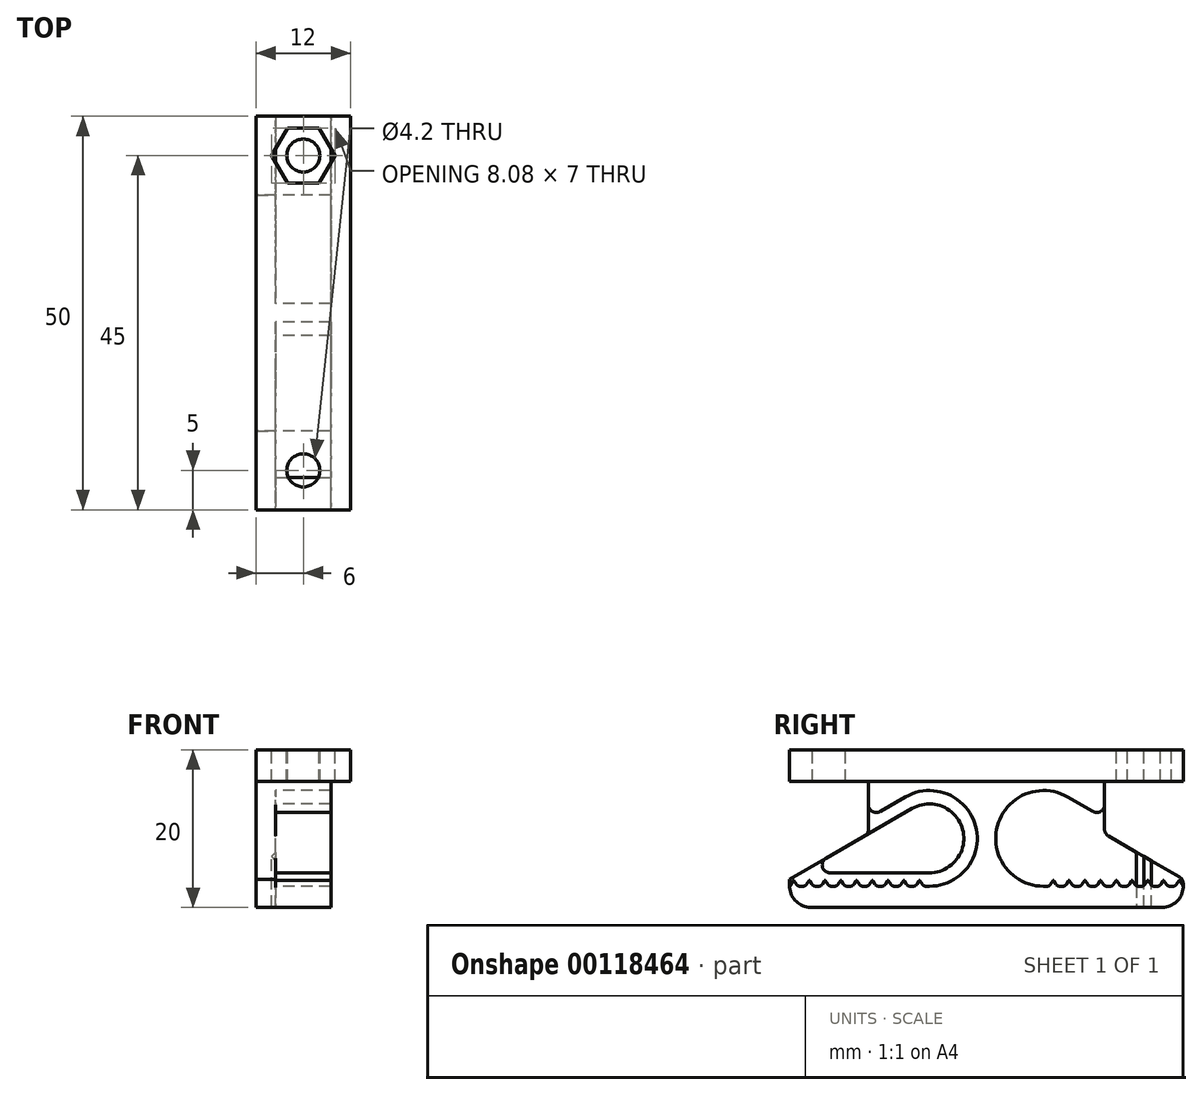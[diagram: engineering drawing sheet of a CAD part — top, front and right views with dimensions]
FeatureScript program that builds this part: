
annotation { "Feature Type Name" : "Feature", "Feature Type Description" : "" }
export const myFeature = defineFeature(function(context is Context, id is Id, definition is map)
    precondition{}
    {
        {
            var Q0;
            Q0=qCreatedBy(makeId("Right.planeOp"),FACE);
            var sketch = newSketch(context, id + "F0", { "sketchPlane" : qUnion([Q0])});
            skLineSegment(sketch, "E0", {"start": v(-25, 0) * mm, "end": v(25, 0) * mm});
            skPoint(sketch, "E1", {"position": v(0, 0) * mm});
            skPoint(sketch, "E2", {"position": v(-20, 0) * mm});
            skPoint(sketch, "E3.MirrorP", {"position": v(20, 0) * mm});
            skLineSegment(sketch, "E4", {"start": v(-25, -16) * mm, "end": v(25, -16) * mm, "construction": true});
            skCircle(sketch, "E5", {"center": v(-7.25, -11.25) * mm, "radius": 4.75 * mm, "construction": true});
            skLineSegment(sketch, "E6", {"start": v(-25, -16) * mm, "end": v(-9.63, -7.13) * mm, "construction": true});
            skCircle(sketch, "E7.MirrorC", {"center": v(7.25, -11.25) * mm, "radius": 4.75 * mm, "construction": true});
            skLineSegment(sketch, "E8.MirrorCS", {"start": v(25, -16) * mm, "end": v(9.63, -7.13) * mm, "construction": true});
            skLineSegment(sketch, "E9", {"start": v(-25, -4) * mm, "end": v(25, -4) * mm});
            skLineSegment(sketch, "E10", {"start": v(25, -4) * mm, "end": v(25, 0) * mm});
            skLineSegment(sketch, "E11.MirrorCS", {"start": v(-25, -4) * mm, "end": v(-25, 0) * mm});
            skLineSegment(sketch, "E12", {"start": v(-25, -20) * mm, "end": v(25, -20) * mm});
            skLineSegment(sketch, "E13", {"start": v(25, -20) * mm, "end": v(25, -16) * mm});
            skLineSegment(sketch, "E14", {"start": v(25, -16) * mm, "end": v(25, -4) * mm});
            skLineSegment(sketch, "E15.MirrorCS", {"start": v(-25, -16) * mm, "end": v(-25, -4) * mm});
            skLineSegment(sketch, "E16.MirrorCS", {"start": v(-25, -20) * mm, "end": v(-25, -16) * mm});
            skLineSegment(sketch, "E17", {"start": v(-15, 0) * mm, "end": v(-15, -20) * mm, "construction": true});
            skLineSegment(sketch, "E18.MirrorCS", {"start": v(15, 0) * mm, "end": v(15, -20) * mm, "construction": true});
            skSolve(sketch);
        }
        {
            var Q0;
            Q0=makeQuery(id+"F0.imprint","IMPRINT",FACE,{"disambiguationData":[TD([[makeQuery(id+"F0.imprint","IMPRINT",EDGE,{"derivedFrom":sQuery(id+"F0.wireOp",EDGE,"E0")}),-1.0]])]});
            extrude(context, id + "F1", {"entities" : qUnion([Q0]), "endBound" : BoundingType.SYMMETRIC, "depth" : 12 * mm});
        }
        {
            var Q0;
            Q0=makeQuery(id+"F0.imprint","IMPRINT",FACE,{"disambiguationData":[TD([[makeQuery(id+"F0.imprint","IMPRINT",EDGE,{"derivedFrom":sQuery(id+"F0.wireOp",EDGE,"E9")}),-1.0]])]});
            var Q1;
            Q1=makeQuery(id+"F1.opExtrude","CAP_FACE",FACE,{"disambiguationData":[OSD([sQuery(id+"F0.wireOp",EDGE,"E0"),sQuery(id+"F0.wireOp",EDGE,"E9"),sQuery(id+"F0.wireOp",EDGE,"E10"),sQuery(id+"F0.wireOp",EDGE,"E11.MirrorCS")])],"isStart":true});
            extrude(context, id + "F2", {"entities" : qUnion([Q0]), "operationType" : NewBodyOperationType.ADD, "endBound" : BoundingType.UP_TO_SURFACE, "oppositeDirection" : true, "endBoundEntityFace" : qUnion([Q1]), "depth" : 25 * mm, "hasSecondDirection" : true, "secondDirectionOppositeDirection" : true, "secondDirectionDepth" : 3.5 * mm});
        }
        {
            var Q0;
            Q0=qCreatedBy(makeId("Top.planeOp"),FACE);
            var sketch = newSketch(context, id + "F3", { "sketchPlane" : qUnion([Q0])});
            skCircle(sketch, "E19.cCircle", {"center": v(0, -20) * mm, "radius": 3.5 * mm, "construction": true});
            skLineSegment(sketch, "E19.0", {"start": v(4.04, -20) * mm, "end": v(2.02, -23.5) * mm});
            skLineSegment(sketch, "E19.1", {"start": v(2.02, -23.5) * mm, "end": v(-2.02, -23.5) * mm});
            skLineSegment(sketch, "E19.2", {"start": v(-2.02, -23.5) * mm, "end": v(-4.04, -20) * mm});
            skLineSegment(sketch, "E19.3", {"start": v(-4.04, -20) * mm, "end": v(-2.02, -16.5) * mm});
            skLineSegment(sketch, "E19.4", {"start": v(-2.02, -16.5) * mm, "end": v(2.02, -16.5) * mm});
            skLineSegment(sketch, "E19.5", {"start": v(2.02, -16.5) * mm, "end": v(4.04, -20) * mm});
            skPoint(sketch, "E19.0.midPoint", {"position": v(3.03, -21.75) * mm});
            skCircle(sketch, "E20", {"center": v(0, -20) * mm, "radius": 2.1 * mm});
            skLineSegment(sketch, "E21", {"start": v(2.02, -16.5) * mm, "end": v(6, -16.5) * mm});
            skLineSegment(sketch, "E22", {"start": v(6, -16.5) * mm, "end": v(6, -23.5) * mm});
            skLineSegment(sketch, "E23", {"start": v(6, -23.5) * mm, "end": v(2.02, -23.5) * mm});
            skLineSegment(sketch, "E24.MirrorCS", {"start": v(-4.04, 20) * mm, "end": v(-2.02, 16.5) * mm});
            skLineSegment(sketch, "E25.MirrorCS", {"start": v(-2.02, 16.5) * mm, "end": v(2.02, 16.5) * mm});
            skLineSegment(sketch, "E26.MirrorCS", {"start": v(2.02, 16.5) * mm, "end": v(6, 16.5) * mm});
            skLineSegment(sketch, "E27.MirrorCS", {"start": v(6, 16.5) * mm, "end": v(6, 23.5) * mm});
            skLineSegment(sketch, "E28.MirrorCS", {"start": v(6, 23.5) * mm, "end": v(2.02, 23.5) * mm});
            skLineSegment(sketch, "E29.MirrorCS", {"start": v(2.02, 23.5) * mm, "end": v(-2.02, 23.5) * mm});
            skLineSegment(sketch, "E30.MirrorCS", {"start": v(-2.02, 23.5) * mm, "end": v(-4.04, 20) * mm});
            skLineSegment(sketch, "E31.MirrorCS", {"start": v(4.04, 20) * mm, "end": v(2.02, 23.5) * mm});
            skLineSegment(sketch, "E32.MirrorCS", {"start": v(2.02, 16.5) * mm, "end": v(4.04, 20) * mm});
            skCircle(sketch, "E33.MirrorC", {"center": v(0, 20) * mm, "radius": 2.1 * mm});
            skSolve(sketch);
        }
        {
            var Q0;
            Q0=makeQuery(id+"F1.opExtrude","SWEPT_BODY",BODY,{"disambiguationData":[OSD([sQuery(id+"F0.wireOp",EDGE,"E0"),sQuery(id+"F0.wireOp",EDGE,"E9"),sQuery(id+"F0.wireOp",EDGE,"E10"),sQuery(id+"F0.wireOp",EDGE,"E11.MirrorCS")])]});
            transform(context, id + "F4", {"entities" : qUnion([Q0]), "transformType" : TransformType.COPY});
        }
        {
            var Q0;
            Q0=makeQuery(id+"F3.imprint","IMPRINT",FACE,{"disambiguationData":[TD([[makeQuery(id+"F3.imprint","IMPRINT",EDGE,{"derivedFrom":sQuery(id+"F3.wireOp",EDGE,"E20")}),1.0]])]});
            var Q1;
            Q1=makeQuery(id+"F3.imprint","IMPRINT",FACE,{"disambiguationData":[TD([[makeQuery(id+"F3.imprint","IMPRINT",EDGE,{"derivedFrom":sQuery(id+"F3.wireOp",EDGE,"E33.MirrorC")}),-1.0]])]});
            extrude(context, id + "F5", {"entities" : qUnion([Q0, Q1]), "operationType" : NewBodyOperationType.REMOVE, "endBound" : BoundingType.THROUGH_ALL, "oppositeDirection" : true, "depth" : 25 * mm});
        }
        {
            var Q0;
            Q0=qCreatedBy(makeId("Right.planeOp"),FACE);
            var sketch = newSketch(context, id + "F6", { "sketchPlane" : qUnion([Q0])});
            skLineSegment(sketch, "E34", {"start": v(-25, -16) * mm, "end": v(-9.63, -7.13) * mm, "construction": true});
            skLineSegment(sketch, "E35", {"start": v(-25, -16) * mm, "end": v(-7.25, -16) * mm, "construction": true});
            skArc(sketch, "E36", {"start": v(-9.63, -7.13) * mm, "mid": v(-11.85, -12.48) * mm, "end": v(-7.25, -16) * mm, "construction": true});
            skArc(sketch, "E37", {"start": v(-7.25, -16) * mm, "mid": v(-2.66, -10.01) * mm, "end": v(-9.63, -7.13) * mm, "construction": true});
            skLineSegment(sketch, "E38.0", {"start": v(-23.6, -15.62) * mm, "end": v(-9.44, -7.45) * mm});
            skLineSegment(sketch, "E38.1", {"start": v(-23.6, -15.62) * mm, "end": v(-7.25, -15.62) * mm});
            skArc(sketch, "E38.2", {"start": v(-7.25, -15.62) * mm, "mid": v(-3.02, -10.11) * mm, "end": v(-9.44, -7.45) * mm});
            skArc(sketch, "E39.MirrorCS", {"start": v(7.25, -15.62) * mm, "mid": v(3.02, -10.11) * mm, "end": v(9.44, -7.45) * mm});
            skLineSegment(sketch, "E40.MirrorCS", {"start": v(23.6, -15.62) * mm, "end": v(7.25, -15.62) * mm});
            skLineSegment(sketch, "E41.MirrorCS", {"start": v(23.6, -15.62) * mm, "end": v(9.44, -7.45) * mm});
            skLineSegment(sketch, "E42.0", {"start": v(-29.94, -17.32) * mm, "end": v(-15, -8.7) * mm, "construction": true});
            skLineSegment(sketch, "E42.1", {"start": v(-29.94, -17.32) * mm, "end": v(-25, -17.32) * mm, "construction": true});
            skArc(sketch, "E42.2", {"start": v(-7.25, -17.32) * mm, "mid": v(-1.38, -9.67) * mm, "end": v(-10.3, -5.98) * mm});
            skLineSegment(sketch, "E43", {"start": v(-15, -4) * mm, "end": v(15, -4) * mm});
            skLineSegment(sketch, "E44", {"start": v(-15, -4) * mm, "end": v(-15, -8.7) * mm});
            skLineSegment(sketch, "E45", {"start": v(-25, -17.32) * mm, "end": v(-25, -20) * mm});
            skLineSegment(sketch, "E46", {"start": v(-25, -20) * mm, "end": v(25, -20) * mm});
            skLineSegment(sketch, "E47", {"start": v(-15, -8.7) * mm, "end": v(-10.3, -5.98) * mm});
            skLineSegment(sketch, "E48", {"start": v(-25, -17.32) * mm, "end": v(-7.25, -17.32) * mm});
            skLineSegment(sketch, "E49.MirrorCS", {"start": v(25, -17.32) * mm, "end": v(25, -20) * mm});
            skLineSegment(sketch, "E50.MirrorCS", {"start": v(25, -17.32) * mm, "end": v(7.25, -17.32) * mm});
            skArc(sketch, "E51.MirrorCS", {"start": v(7.25, -17.32) * mm, "mid": v(1.38, -9.67) * mm, "end": v(10.3, -5.98) * mm});
            skLineSegment(sketch, "E52.MirrorCS", {"start": v(15, -8.7) * mm, "end": v(10.3, -5.98) * mm});
            skLineSegment(sketch, "E53.MirrorCS", {"start": v(15, -4) * mm, "end": v(15, -8.7) * mm});
            skArc(sketch, "E54", {"start": v(-25, -17.32) * mm, "mid": v(-24.22, -19.22) * mm, "end": v(-22.33, -20) * mm});
            skLineSegment(sketch, "E55", {"start": v(-24.5, -16.65) * mm, "end": v(-24.5, -17.32) * mm, "construction": true});
            skLineSegment(sketch, "E56", {"start": v(-25, -17.32) * mm, "end": v(-24.56, -16.61) * mm});
            skLineSegment(sketch, "E57.MirrorCS", {"start": v(-24, -17.32) * mm, "end": v(-24.44, -16.61) * mm});
            skArc(sketch, "E58", {"start": v(-24.56, -16.61) * mm, "mid": v(-24.5, -16.73) * mm, "end": v(-24.44, -16.61) * mm, "construction": true});
            skArc(sketch, "E59", {"start": v(-24.44, -16.61) * mm, "mid": v(-24.5, -16.58) * mm, "end": v(-24.56, -16.61) * mm});
            skLineSegment(sketch, "E60.1.0.0", {"start": v(-23, -17.33) * mm, "end": v(-22.56, -16.61) * mm});
            skArc(sketch, "E60.1.0.1", {"start": v(-22.44, -16.61) * mm, "mid": v(-22.5, -16.58) * mm, "end": v(-22.56, -16.61) * mm});
            skLineSegment(sketch, "E60.1.0.2", {"start": v(-22, -17.32) * mm, "end": v(-22.44, -16.61) * mm});
            skLineSegment(sketch, "E60.2.0.0", {"start": v(-21, -17.32) * mm, "end": v(-20.56, -16.61) * mm});
            skArc(sketch, "E60.2.0.1", {"start": v(-20.44, -16.61) * mm, "mid": v(-20.5, -16.58) * mm, "end": v(-20.56, -16.61) * mm});
            skLineSegment(sketch, "E60.2.0.2", {"start": v(-20, -17.32) * mm, "end": v(-20.44, -16.61) * mm});
            skLineSegment(sketch, "E60.3.0.0", {"start": v(-19, -17.32) * mm, "end": v(-18.56, -16.61) * mm});
            skArc(sketch, "E60.3.0.1", {"start": v(-18.44, -16.61) * mm, "mid": v(-18.5, -16.58) * mm, "end": v(-18.56, -16.61) * mm});
            skLineSegment(sketch, "E60.3.0.2", {"start": v(-18, -17.32) * mm, "end": v(-18.44, -16.61) * mm});
            skLineSegment(sketch, "E60.4.0.0", {"start": v(-17, -17.32) * mm, "end": v(-16.56, -16.61) * mm});
            skArc(sketch, "E60.4.0.1", {"start": v(-16.44, -16.61) * mm, "mid": v(-16.5, -16.58) * mm, "end": v(-16.56, -16.61) * mm});
            skLineSegment(sketch, "E60.4.0.2", {"start": v(-16, -17.32) * mm, "end": v(-16.44, -16.61) * mm});
            skLineSegment(sketch, "E60.5.0.0", {"start": v(-15, -17.32) * mm, "end": v(-14.56, -16.61) * mm});
            skArc(sketch, "E60.5.0.1", {"start": v(-14.44, -16.61) * mm, "mid": v(-14.5, -16.57) * mm, "end": v(-14.56, -16.61) * mm});
            skLineSegment(sketch, "E60.5.0.2", {"start": v(-14, -17.32) * mm, "end": v(-14.44, -16.61) * mm});
            skLineSegment(sketch, "E60.6.0.0", {"start": v(-13, -17.32) * mm, "end": v(-12.56, -16.61) * mm});
            skArc(sketch, "E60.6.0.1", {"start": v(-12.44, -16.61) * mm, "mid": v(-12.5, -16.57) * mm, "end": v(-12.56, -16.61) * mm});
            skLineSegment(sketch, "E60.6.0.2", {"start": v(-12, -17.32) * mm, "end": v(-12.44, -16.61) * mm});
            skLineSegment(sketch, "E60.7.0.0", {"start": v(-11, -17.32) * mm, "end": v(-10.56, -16.61) * mm});
            skArc(sketch, "E60.7.0.1", {"start": v(-10.44, -16.61) * mm, "mid": v(-10.5, -16.57) * mm, "end": v(-10.56, -16.61) * mm});
            skLineSegment(sketch, "E60.7.0.2", {"start": v(-10, -17.32) * mm, "end": v(-10.44, -16.61) * mm});
            skLineSegment(sketch, "E60.8.0.0", {"start": v(-9, -17.32) * mm, "end": v(-8.56, -16.61) * mm});
            skArc(sketch, "E60.8.0.1", {"start": v(-8.44, -16.61) * mm, "mid": v(-8.5, -16.57) * mm, "end": v(-8.56, -16.61) * mm});
            skLineSegment(sketch, "E60.8.0.2", {"start": v(-8, -17.32) * mm, "end": v(-8.44, -16.61) * mm});
            skLineSegment(sketch, "E60.direction1", {"start": v(-25, -17.32) * mm, "end": v(-23, -17.32) * mm, "construction": true});
            skArc(sketch, "E61.MirrorCS", {"start": v(25, -17.32) * mm, "mid": v(24.22, -19.22) * mm, "end": v(22.33, -20) * mm});
            skLineSegment(sketch, "E62.MirrorCS", {"start": v(25, -17.32) * mm, "end": v(24.56, -16.61) * mm});
            skArc(sketch, "E63.MirrorCS", {"start": v(24.44, -16.61) * mm, "mid": v(24.5, -16.58) * mm, "end": v(24.56, -16.61) * mm});
            skLineSegment(sketch, "E64.MirrorCS", {"start": v(24, -17.32) * mm, "end": v(24.44, -16.61) * mm});
            skLineSegment(sketch, "E65.MirrorCS", {"start": v(23, -17.33) * mm, "end": v(22.56, -16.61) * mm});
            skLineSegment(sketch, "E66.MirrorCS", {"start": v(22, -17.32) * mm, "end": v(22.44, -16.61) * mm});
            skLineSegment(sketch, "E67.MirrorCS", {"start": v(21, -17.32) * mm, "end": v(20.56, -16.61) * mm});
            skLineSegment(sketch, "E68.MirrorCS", {"start": v(20, -17.32) * mm, "end": v(20.44, -16.61) * mm});
            skArc(sketch, "E69.MirrorCS", {"start": v(20.44, -16.61) * mm, "mid": v(20.5, -16.58) * mm, "end": v(20.56, -16.61) * mm});
            skArc(sketch, "E70.MirrorCS", {"start": v(22.44, -16.61) * mm, "mid": v(22.5, -16.58) * mm, "end": v(22.56, -16.61) * mm});
            skLineSegment(sketch, "E71.MirrorCS", {"start": v(19, -17.32) * mm, "end": v(18.56, -16.61) * mm});
            skArc(sketch, "E72.MirrorCS", {"start": v(18.44, -16.61) * mm, "mid": v(18.5, -16.58) * mm, "end": v(18.56, -16.61) * mm});
            skLineSegment(sketch, "E73.MirrorCS", {"start": v(18, -17.32) * mm, "end": v(18.44, -16.61) * mm});
            skLineSegment(sketch, "E74.MirrorCS", {"start": v(17, -17.32) * mm, "end": v(16.56, -16.61) * mm});
            skArc(sketch, "E75.MirrorCS", {"start": v(16.44, -16.61) * mm, "mid": v(16.5, -16.58) * mm, "end": v(16.56, -16.61) * mm});
            skLineSegment(sketch, "E76.MirrorCS", {"start": v(16, -17.32) * mm, "end": v(16.44, -16.61) * mm});
            skLineSegment(sketch, "E77.MirrorCS", {"start": v(15, -17.32) * mm, "end": v(14.56, -16.61) * mm});
            skArc(sketch, "E78.MirrorCS", {"start": v(14.44, -16.61) * mm, "mid": v(14.5, -16.57) * mm, "end": v(14.56, -16.61) * mm});
            skLineSegment(sketch, "E79.MirrorCS", {"start": v(14, -17.32) * mm, "end": v(14.44, -16.61) * mm});
            skLineSegment(sketch, "E80.MirrorCS", {"start": v(13, -17.32) * mm, "end": v(12.56, -16.61) * mm});
            skArc(sketch, "E81.MirrorCS", {"start": v(12.44, -16.61) * mm, "mid": v(12.5, -16.57) * mm, "end": v(12.56, -16.61) * mm});
            skLineSegment(sketch, "E82.MirrorCS", {"start": v(12, -17.32) * mm, "end": v(12.44, -16.61) * mm});
            skLineSegment(sketch, "E83.MirrorCS", {"start": v(11, -17.32) * mm, "end": v(10.56, -16.61) * mm});
            skArc(sketch, "E84.MirrorCS", {"start": v(10.44, -16.61) * mm, "mid": v(10.5, -16.57) * mm, "end": v(10.56, -16.61) * mm});
            skLineSegment(sketch, "E85.MirrorCS", {"start": v(10, -17.32) * mm, "end": v(10.44, -16.61) * mm});
            skLineSegment(sketch, "E86.MirrorCS", {"start": v(9, -17.32) * mm, "end": v(8.56, -16.61) * mm});
            skArc(sketch, "E87.MirrorCS", {"start": v(8.44, -16.61) * mm, "mid": v(8.5, -16.57) * mm, "end": v(8.56, -16.61) * mm});
            skLineSegment(sketch, "E88.MirrorCS", {"start": v(8, -17.32) * mm, "end": v(8.44, -16.61) * mm});
            skLineSegment(sketch, "E89", {"start": v(-23.6, -15.62) * mm, "end": v(-25, -16.43) * mm});
            skLineSegment(sketch, "E90", {"start": v(-25, -16.43) * mm, "end": v(-25, -4) * mm});
            skLineSegment(sketch, "E91", {"start": v(-25, -4) * mm, "end": v(-15, -4) * mm});
            skLineSegment(sketch, "E92", {"start": v(-15, -8.7) * mm, "end": v(-15, -10.66) * mm});
            skLineSegment(sketch, "E93.MirrorCS", {"start": v(15, -8.7) * mm, "end": v(15, -10.66) * mm});
            skLineSegment(sketch, "E94.MirrorCS", {"start": v(25, -4) * mm, "end": v(15, -4) * mm});
            skLineSegment(sketch, "E95.MirrorCS", {"start": v(25, -16.43) * mm, "end": v(25, -4) * mm});
            skLineSegment(sketch, "E96.MirrorCS", {"start": v(23.6, -15.62) * mm, "end": v(25, -16.43) * mm});
            skSolve(sketch);
        }
        {
            var Q0;
            Q0=makeQuery(id+"F4.opPattern","COPY",BODY,{"derivedFrom":makeQuery(id+"F1.opExtrude","SWEPT_BODY",BODY,{"disambiguationData":[OSD([sQuery(id+"F0.wireOp",EDGE,"E0"),sQuery(id+"F0.wireOp",EDGE,"E9"),sQuery(id+"F0.wireOp",EDGE,"E10"),sQuery(id+"F0.wireOp",EDGE,"E11.MirrorCS")])]}),"instanceName":"1"});
            transform(context, id + "F7", {"entities" : qUnion([Q0]), "transformType" : TransformType.COPY});
        }
        {
            var Q0;
            {var subQ31=sQuery(id+"F6.wireOp",EDGE,"E42.2");Q0=makeQuery(id+"F6.imprint","IMPRINT",FACE,{"disambiguationData":[TD([[makeQuery(id+"F6.imprint","IMPRINT",EDGE,{"derivedFrom":subQ31}),-1.0]])]});}
            var Q1;
            Q1=makeQuery(id+"F6.imprint","IMPRINT",FACE,{"disambiguationData":[TD([[makeQuery(id+"F6.imprint","IMPRINT",EDGE,{"derivedFrom":sQuery(id+"F6.wireOp",EDGE,"E38.0")}),-1.0]])]});
            var Q2;
            Q2=makeQuery(id+"F6.imprint","IMPRINT",FACE,{"disambiguationData":[TD([[makeQuery(id+"F6.imprint","IMPRINT",EDGE,{"derivedFrom":sQuery(id+"F6.wireOp",EDGE,"E39.MirrorCS")}),-1.0]])]});
            var Q3;
            {var subQ0=sQuery(id+"F6.wireOp",EDGE,"E56");Q3=makeQuery(id+"F6.imprint","IMPRINT",FACE,{"disambiguationData":[TD([[makeQuery(id+"F6.imprint","IMPRINT",EDGE,{"derivedFrom":subQ0}),-1.0]])]});}
            var Q4;
            {var subQ0=sQuery(id+"F6.wireOp",EDGE,"E60.1.0.0");Q4=makeQuery(id+"F6.imprint","IMPRINT",FACE,{"disambiguationData":[TD([[makeQuery(id+"F6.imprint","IMPRINT",EDGE,{"derivedFrom":subQ0}),-1.0]])]});}
            var Q5;
            {var subQ0=sQuery(id+"F6.wireOp",EDGE,"E60.2.0.0");Q5=makeQuery(id+"F6.imprint","IMPRINT",FACE,{"disambiguationData":[TD([[makeQuery(id+"F6.imprint","IMPRINT",EDGE,{"derivedFrom":subQ0}),-1.0]])]});}
            var Q6;
            {var subQ0=sQuery(id+"F6.wireOp",EDGE,"E60.3.0.0");Q6=makeQuery(id+"F6.imprint","IMPRINT",FACE,{"disambiguationData":[TD([[makeQuery(id+"F6.imprint","IMPRINT",EDGE,{"derivedFrom":subQ0}),-1.0]])]});}
            var Q7;
            {var subQ0=sQuery(id+"F6.wireOp",EDGE,"E60.4.0.0");Q7=makeQuery(id+"F6.imprint","IMPRINT",FACE,{"disambiguationData":[TD([[makeQuery(id+"F6.imprint","IMPRINT",EDGE,{"derivedFrom":subQ0}),-1.0]])]});}
            var Q8;
            {var subQ0=sQuery(id+"F6.wireOp",EDGE,"E60.5.0.0");Q8=makeQuery(id+"F6.imprint","IMPRINT",FACE,{"disambiguationData":[TD([[makeQuery(id+"F6.imprint","IMPRINT",EDGE,{"derivedFrom":subQ0}),-1.0]])]});}
            var Q9;
            {var subQ0=sQuery(id+"F6.wireOp",EDGE,"E60.6.0.0");Q9=makeQuery(id+"F6.imprint","IMPRINT",FACE,{"disambiguationData":[TD([[makeQuery(id+"F6.imprint","IMPRINT",EDGE,{"derivedFrom":subQ0}),-1.0]])]});}
            var Q10;
            {var subQ0=sQuery(id+"F6.wireOp",EDGE,"E60.7.0.0");Q10=makeQuery(id+"F6.imprint","IMPRINT",FACE,{"disambiguationData":[TD([[makeQuery(id+"F6.imprint","IMPRINT",EDGE,{"derivedFrom":subQ0}),-1.0]])]});}
            var Q11;
            {var subQ0=sQuery(id+"F6.wireOp",EDGE,"E60.8.0.0");Q11=makeQuery(id+"F6.imprint","IMPRINT",FACE,{"disambiguationData":[TD([[makeQuery(id+"F6.imprint","IMPRINT",EDGE,{"derivedFrom":subQ0}),-1.0]])]});}
            var Q12;
            {var subQ0=sQuery(id+"F6.wireOp",EDGE,"E86.MirrorCS");Q12=makeQuery(id+"F6.imprint","IMPRINT",FACE,{"disambiguationData":[TD([[makeQuery(id+"F6.imprint","IMPRINT",EDGE,{"derivedFrom":subQ0}),1.0]])]});}
            var Q13;
            {var subQ0=sQuery(id+"F6.wireOp",EDGE,"E83.MirrorCS");Q13=makeQuery(id+"F6.imprint","IMPRINT",FACE,{"disambiguationData":[TD([[makeQuery(id+"F6.imprint","IMPRINT",EDGE,{"derivedFrom":subQ0}),1.0]])]});}
            var Q14;
            {var subQ0=sQuery(id+"F6.wireOp",EDGE,"E80.MirrorCS");Q14=makeQuery(id+"F6.imprint","IMPRINT",FACE,{"disambiguationData":[TD([[makeQuery(id+"F6.imprint","IMPRINT",EDGE,{"derivedFrom":subQ0}),1.0]])]});}
            var Q15;
            {var subQ0=sQuery(id+"F6.wireOp",EDGE,"E77.MirrorCS");Q15=makeQuery(id+"F6.imprint","IMPRINT",FACE,{"disambiguationData":[TD([[makeQuery(id+"F6.imprint","IMPRINT",EDGE,{"derivedFrom":subQ0}),1.0]])]});}
            var Q16;
            {var subQ0=sQuery(id+"F6.wireOp",EDGE,"E74.MirrorCS");Q16=makeQuery(id+"F6.imprint","IMPRINT",FACE,{"disambiguationData":[TD([[makeQuery(id+"F6.imprint","IMPRINT",EDGE,{"derivedFrom":subQ0}),1.0]])]});}
            var Q17;
            {var subQ0=sQuery(id+"F6.wireOp",EDGE,"E71.MirrorCS");Q17=makeQuery(id+"F6.imprint","IMPRINT",FACE,{"disambiguationData":[TD([[makeQuery(id+"F6.imprint","IMPRINT",EDGE,{"derivedFrom":subQ0}),1.0]])]});}
            var Q18;
            {var subQ0=sQuery(id+"F6.wireOp",EDGE,"E67.MirrorCS");Q18=makeQuery(id+"F6.imprint","IMPRINT",FACE,{"disambiguationData":[TD([[makeQuery(id+"F6.imprint","IMPRINT",EDGE,{"derivedFrom":subQ0}),1.0]])]});}
            var Q19;
            {var subQ0=sQuery(id+"F6.wireOp",EDGE,"E65.MirrorCS");Q19=makeQuery(id+"F6.imprint","IMPRINT",FACE,{"disambiguationData":[TD([[makeQuery(id+"F6.imprint","IMPRINT",EDGE,{"derivedFrom":subQ0}),1.0]])]});}
            var Q20;
            {var subQ0=sQuery(id+"F6.wireOp",EDGE,"E62.MirrorCS");Q20=makeQuery(id+"F6.imprint","IMPRINT",FACE,{"disambiguationData":[TD([[makeQuery(id+"F6.imprint","IMPRINT",EDGE,{"derivedFrom":subQ0}),1.0]])]});}
            extrude(context, id + "F8", {"entities" : qUnion([Q0, Q1, Q2, Q3, Q4, Q5, Q6, Q7, Q8, Q9, Q10, Q11, Q12, Q13, Q14, Q15, Q16, Q17, Q18, Q19, Q20]), "operationType" : NewBodyOperationType.ADD, "endBound" : BoundingType.SYMMETRIC, "depth" : 7 * mm});
        }
        {
            var Q0;
            {var subQ0=sQuery(id+"F6.wireOp",EDGE,"E45");Q0=makeQuery(id+"F6.imprint","IMPRINT",FACE,{"disambiguationData":[TD([[makeQuery(id+"F6.imprint","IMPRINT",EDGE,{"derivedFrom":subQ0}),1.0]])]});}
            var Q1;
            {var subQ0=sQuery(id+"F6.wireOp",EDGE,"E49.MirrorCS");Q1=makeQuery(id+"F6.imprint","IMPRINT",FACE,{"disambiguationData":[TD([[makeQuery(id+"F6.imprint","IMPRINT",EDGE,{"derivedFrom":subQ0}),-1.0]])]});}
            var Q2;
            Q2=makeQuery(id+"F6.imprint","IMPRINT",FACE,{"disambiguationData":[TD([[makeQuery(id+"F6.imprint","IMPRINT",EDGE,{"derivedFrom":sQuery(id+"F6.wireOp",EDGE,"E44")}),-1.0]])]});
            var Q3;
            Q3=makeQuery(id+"F6.imprint","IMPRINT",FACE,{"disambiguationData":[TD([[makeQuery(id+"F6.imprint","IMPRINT",EDGE,{"derivedFrom":sQuery(id+"F6.wireOp",EDGE,"E53.MirrorCS")}),1.0]])]});
            extrude(context, id + "F9", {"entities" : qUnion([Q0, Q1, Q2, Q3]), "operationType" : NewBodyOperationType.REMOVE, "endBound" : BoundingType.THROUGH_ALL, "oppositeDirection" : true, "depth" : 25 * mm});
        }
        {
            var Q0;
            Q0=makeQuery(id+"F8.opExtrude","SWEPT_EDGE",EDGE,{"disambiguationData":[OSD([sQuery(id+"F6.wireOp",EDGE,"E38.0"),sQuery(id+"F6.wireOp",EDGE,"E38.1")])]});
            var Q1;
            Q1=makeQuery(id+"F8.opExtrude","SWEPT_EDGE",EDGE,{"disambiguationData":[OSD([sQuery(id+"F6.wireOp",EDGE,"E40.MirrorCS"),sQuery(id+"F6.wireOp",EDGE,"E41.MirrorCS")])]});
            var Q2;
            Q2=makeQuery(id+"F8.opExtrude","SWEPT_EDGE",EDGE,{"disambiguationData":[OSD([sQuery(id+"F6.wireOp",EDGE,"E44"),sQuery(id+"F6.wireOp",EDGE,"E47")])]});
            var Q3;
            Q3=makeQuery(id+"F8.opExtrude","SWEPT_EDGE",EDGE,{"disambiguationData":[OSD([sQuery(id+"F6.wireOp",EDGE,"E52.MirrorCS"),sQuery(id+"F6.wireOp",EDGE,"E53.MirrorCS")])]});
            var Q4;
            Q4=makeQuery(id+"F8.opExtrude","SWEPT_EDGE",EDGE,{"disambiguationData":[OSD([sQuery(id+"F6.wireOp",EDGE,"E43"),sQuery(id+"F6.wireOp",EDGE,"E44")])]});
            var Q5;
            Q5=makeQuery(id+"F8.opExtrude","SWEPT_EDGE",EDGE,{"disambiguationData":[OSD([sQuery(id+"F6.wireOp",EDGE,"E43"),sQuery(id+"F6.wireOp",EDGE,"E53.MirrorCS")])]});
            var Q6;
            Q6=makeQuery(id+"F7.opPattern","COPY",EDGE,{"derivedFrom":makeQuery(id+"F4.opPattern","COPY",EDGE,{"derivedFrom":makeQuery(id+"F1.opExtrude","SWEPT_EDGE",EDGE,{"disambiguationData":[OSD([sQuery(id+"F0.wireOp",EDGE,"E9"),sQuery(id+"F0.wireOp",EDGE,"E11.MirrorCS"),sQuery(id+"F0.wireOp",EDGE,"E15.MirrorCS")])]}),"instanceName":"1"}),"instanceName":"1"});
            var Q7;
            Q7=makeQuery(id+"F7.opPattern","COPY",EDGE,{"derivedFrom":makeQuery(id+"F4.opPattern","COPY",EDGE,{"derivedFrom":makeQuery(id+"F1.opExtrude","SWEPT_EDGE",EDGE,{"disambiguationData":[OSD([sQuery(id+"F0.wireOp",EDGE,"E9"),sQuery(id+"F0.wireOp",EDGE,"E10"),sQuery(id+"F0.wireOp",EDGE,"E14")])]}),"instanceName":"1"}),"instanceName":"1"});
            var Q8;
            Q8=makeQuery(id+"F9.boolean.opBoolean","COPY",EDGE,{"derivedFrom":makeQuery(id+"F9.opExtrude","SWEPT_EDGE",EDGE,{"disambiguationData":[OSD([sQuery(id+"F6.wireOp",EDGE,"E89"),sQuery(id+"F6.wireOp",EDGE,"E90")])]})});
            var Q9;
            Q9=makeQuery(id+"F9.boolean.opBoolean","COPY",EDGE,{"derivedFrom":makeQuery(id+"F9.opExtrude","SWEPT_EDGE",EDGE,{"disambiguationData":[OSD([sQuery(id+"F6.wireOp",EDGE,"E95.MirrorCS"),sQuery(id+"F6.wireOp",EDGE,"E96.MirrorCS")])]})});
            var Q10;
            Q10=makeQuery(id+"F9.boolean.opBoolean","COPY",EDGE,{"derivedFrom":makeQuery(id+"F9.opExtrude","SWEPT_EDGE",EDGE,{"disambiguationData":[OSD([sQuery(id+"F6.wireOp",EDGE,"E38.0"),sQuery(id+"F6.wireOp",EDGE,"E92")])]})});
            var Q11;
            Q11=makeQuery(id+"F9.boolean.opBoolean","COPY",EDGE,{"derivedFrom":makeQuery(id+"F9.opExtrude","SWEPT_EDGE",EDGE,{"disambiguationData":[OSD([sQuery(id+"F6.wireOp",EDGE,"E41.MirrorCS"),sQuery(id+"F6.wireOp",EDGE,"E93.MirrorCS")])]})});
            fillet(context, id + "F10", {"entities" : qUnion([Q0, Q1, Q2, Q3, Q4, Q5, Q6, Q7, Q8, Q9, Q10, Q11]), "radius" : 1 * mm, "tangentPropagation" : true, "allowEdgeOverflow" : false});
        }
        {
            var Q0;
            Q0=makeQuery(id+"F7.opPattern","COPY",EDGE,{"derivedFrom":makeQuery(id+"FzJrt3O1qZVC5p7_1.boolean.opBoolean","INTERSECT",EDGE,{"derivedFrom":[makeQuery(id+"F4.opPattern","COPY",FACE,{"derivedFrom":makeQuery(id+"F1.opExtrude","SWEPT_FACE",FACE,{"disambiguationData":[OSD([sQuery(id+"F0.wireOp",EDGE,"E9")])]}),"instanceName":"1"}),makeQuery(id+"FzJrt3O1qZVC5p7_1.opExtrude","SWEPT_FACE",FACE,{"disambiguationData":[OSD([sQuery(id+"F3.wireOp",EDGE,"E19.1"),sQuery(id+"F3.wireOp",EDGE,"E23")])]})]}),"instanceName":"1"});
            var Q1;
            Q1=makeQuery(id+"F7.opPattern","COPY",EDGE,{"derivedFrom":makeQuery(id+"FzJrt3O1qZVC5p7_1.boolean.opBoolean","INTERSECT",EDGE,{"derivedFrom":[makeQuery(id+"F4.opPattern","COPY",FACE,{"derivedFrom":makeQuery(id+"F1.opExtrude","SWEPT_FACE",FACE,{"disambiguationData":[OSD([sQuery(id+"F0.wireOp",EDGE,"E9")])]}),"instanceName":"1"}),makeQuery(id+"FzJrt3O1qZVC5p7_1.opExtrude","SWEPT_FACE",FACE,{"disambiguationData":[OSD([sQuery(id+"F3.wireOp",EDGE,"E19.4"),sQuery(id+"F3.wireOp",EDGE,"E21")])]})]}),"instanceName":"1"});
            var Q2;
            Q2=makeQuery(id+"F7.opPattern","COPY",EDGE,{"derivedFrom":makeQuery(id+"FzJrt3O1qZVC5p7_1.boolean.opBoolean","INTERSECT",EDGE,{"derivedFrom":[makeQuery(id+"F4.opPattern","COPY",FACE,{"derivedFrom":makeQuery(id+"F1.opExtrude","SWEPT_FACE",FACE,{"disambiguationData":[OSD([sQuery(id+"F0.wireOp",EDGE,"E9")])]}),"instanceName":"1"}),makeQuery(id+"FzJrt3O1qZVC5p7_1.opExtrude","SWEPT_FACE",FACE,{"disambiguationData":[OSD([sQuery(id+"F3.wireOp",EDGE,"E19.2")])]})]}),"instanceName":"1"});
            var Q3;
            Q3=makeQuery(id+"F7.opPattern","COPY",EDGE,{"derivedFrom":makeQuery(id+"FzJrt3O1qZVC5p7_1.boolean.opBoolean","INTERSECT",EDGE,{"derivedFrom":[makeQuery(id+"F4.opPattern","COPY",FACE,{"derivedFrom":makeQuery(id+"F1.opExtrude","SWEPT_FACE",FACE,{"disambiguationData":[OSD([sQuery(id+"F0.wireOp",EDGE,"E9")])]}),"instanceName":"1"}),makeQuery(id+"FzJrt3O1qZVC5p7_1.opExtrude","SWEPT_FACE",FACE,{"disambiguationData":[OSD([sQuery(id+"F3.wireOp",EDGE,"E19.3")])]})]}),"instanceName":"1"});
            var Q4;
            Q4=makeQuery(id+"F7.opPattern","COPY",EDGE,{"derivedFrom":makeQuery(id+"FzJrt3O1qZVC5p7_1.boolean.opBoolean","INTERSECT",EDGE,{"derivedFrom":[makeQuery(id+"F4.opPattern","COPY",FACE,{"derivedFrom":makeQuery(id+"F1.opExtrude","SWEPT_FACE",FACE,{"disambiguationData":[OSD([sQuery(id+"F0.wireOp",EDGE,"E9")])]}),"instanceName":"1"}),makeQuery(id+"FzJrt3O1qZVC5p7_1.opExtrude","SWEPT_FACE",FACE,{"disambiguationData":[OSD([sQuery(id+"F3.wireOp",EDGE,"E25.MirrorCS"),sQuery(id+"F3.wireOp",EDGE,"E26.MirrorCS")])]})]}),"instanceName":"1"});
            var Q5;
            Q5=makeQuery(id+"F7.opPattern","COPY",EDGE,{"derivedFrom":makeQuery(id+"FzJrt3O1qZVC5p7_1.boolean.opBoolean","INTERSECT",EDGE,{"derivedFrom":[makeQuery(id+"F4.opPattern","COPY",FACE,{"derivedFrom":makeQuery(id+"F1.opExtrude","SWEPT_FACE",FACE,{"disambiguationData":[OSD([sQuery(id+"F0.wireOp",EDGE,"E9")])]}),"instanceName":"1"}),makeQuery(id+"FzJrt3O1qZVC5p7_1.opExtrude","SWEPT_FACE",FACE,{"disambiguationData":[OSD([sQuery(id+"F3.wireOp",EDGE,"E24.MirrorCS")])]})]}),"instanceName":"1"});
            var Q6;
            Q6=makeQuery(id+"F7.opPattern","COPY",EDGE,{"derivedFrom":makeQuery(id+"FzJrt3O1qZVC5p7_1.boolean.opBoolean","INTERSECT",EDGE,{"derivedFrom":[makeQuery(id+"F4.opPattern","COPY",FACE,{"derivedFrom":makeQuery(id+"F1.opExtrude","SWEPT_FACE",FACE,{"disambiguationData":[OSD([sQuery(id+"F0.wireOp",EDGE,"E9")])]}),"instanceName":"1"}),makeQuery(id+"FzJrt3O1qZVC5p7_1.opExtrude","SWEPT_FACE",FACE,{"disambiguationData":[OSD([sQuery(id+"F3.wireOp",EDGE,"E30.MirrorCS")])]})]}),"instanceName":"1"});
            var Q7;
            Q7=makeQuery(id+"F7.opPattern","COPY",EDGE,{"derivedFrom":makeQuery(id+"FzJrt3O1qZVC5p7_1.boolean.opBoolean","INTERSECT",EDGE,{"derivedFrom":[makeQuery(id+"F4.opPattern","COPY",FACE,{"derivedFrom":makeQuery(id+"F1.opExtrude","SWEPT_FACE",FACE,{"disambiguationData":[OSD([sQuery(id+"F0.wireOp",EDGE,"E9")])]}),"instanceName":"1"}),makeQuery(id+"FzJrt3O1qZVC5p7_1.opExtrude","SWEPT_FACE",FACE,{"disambiguationData":[OSD([sQuery(id+"F3.wireOp",EDGE,"E28.MirrorCS"),sQuery(id+"F3.wireOp",EDGE,"E29.MirrorCS")])]})]}),"instanceName":"1"});
            var Q8;
            Q8=makeQuery(id+"F8.opExtrude","SWEPT_EDGE",EDGE,{"disambiguationData":[OSD([sQuery(id+"F6.wireOp",EDGE,"E45"),sQuery(id+"F6.wireOp",EDGE,"E48"),sQuery(id+"F6.wireOp",EDGE,"E54"),sQuery(id+"F6.wireOp",EDGE,"E56")])]});
            var Q9;
            Q9=makeQuery(id+"F8.opExtrude","SWEPT_EDGE",EDGE,{"disambiguationData":[OSD([sQuery(id+"F6.wireOp",EDGE,"E49.MirrorCS"),sQuery(id+"F6.wireOp",EDGE,"E50.MirrorCS"),sQuery(id+"F6.wireOp",EDGE,"E61.MirrorCS"),sQuery(id+"F6.wireOp",EDGE,"E62.MirrorCS")])]});
            var Q10;
            Q10=makeQuery(id+"F8.opExtrude","SWEPT_EDGE",EDGE,{"disambiguationData":[OSD([sQuery(id+"F6.wireOp",EDGE,"E48"),sQuery(id+"F6.wireOp",EDGE,"E57.MirrorCS")])]});
            var Q11;
            Q11=makeQuery(id+"F8.opExtrude","SWEPT_EDGE",EDGE,{"disambiguationData":[OSD([sQuery(id+"F6.wireOp",EDGE,"E48"),sQuery(id+"F6.wireOp",EDGE,"E60.1.0.2")])]});
            var Q12;
            Q12=makeQuery(id+"F8.opExtrude","SWEPT_EDGE",EDGE,{"disambiguationData":[OSD([sQuery(id+"F6.wireOp",EDGE,"E48"),sQuery(id+"F6.wireOp",EDGE,"E60.2.0.2")])]});
            var Q13;
            Q13=makeQuery(id+"F8.opExtrude","SWEPT_EDGE",EDGE,{"disambiguationData":[OSD([sQuery(id+"F6.wireOp",EDGE,"E48"),sQuery(id+"F6.wireOp",EDGE,"E60.3.0.2")])]});
            var Q14;
            Q14=makeQuery(id+"F8.opExtrude","SWEPT_EDGE",EDGE,{"disambiguationData":[OSD([sQuery(id+"F6.wireOp",EDGE,"E48"),sQuery(id+"F6.wireOp",EDGE,"E60.4.0.2")])]});
            var Q15;
            Q15=makeQuery(id+"F8.opExtrude","SWEPT_EDGE",EDGE,{"disambiguationData":[OSD([sQuery(id+"F6.wireOp",EDGE,"E48"),sQuery(id+"F6.wireOp",EDGE,"E60.5.0.2")])]});
            var Q16;
            Q16=makeQuery(id+"F8.opExtrude","SWEPT_EDGE",EDGE,{"disambiguationData":[OSD([sQuery(id+"F6.wireOp",EDGE,"E48"),sQuery(id+"F6.wireOp",EDGE,"E60.6.0.2")])]});
            var Q17;
            Q17=makeQuery(id+"F8.opExtrude","SWEPT_EDGE",EDGE,{"disambiguationData":[OSD([sQuery(id+"F6.wireOp",EDGE,"E48"),sQuery(id+"F6.wireOp",EDGE,"E60.7.0.2")])]});
            var Q18;
            Q18=makeQuery(id+"F8.opExtrude","SWEPT_EDGE",EDGE,{"disambiguationData":[OSD([sQuery(id+"F6.wireOp",EDGE,"E48"),sQuery(id+"F6.wireOp",EDGE,"E60.8.0.2")])]});
            var Q19;
            Q19=makeQuery(id+"F8.opExtrude","SWEPT_EDGE",EDGE,{"disambiguationData":[OSD([sQuery(id+"F6.wireOp",EDGE,"E50.MirrorCS"),sQuery(id+"F6.wireOp",EDGE,"E65.MirrorCS")])]});
            var Q20;
            Q20=makeQuery(id+"F8.opExtrude","SWEPT_EDGE",EDGE,{"disambiguationData":[OSD([sQuery(id+"F6.wireOp",EDGE,"E50.MirrorCS"),sQuery(id+"F6.wireOp",EDGE,"E67.MirrorCS")])]});
            var Q21;
            Q21=makeQuery(id+"F8.opExtrude","SWEPT_EDGE",EDGE,{"disambiguationData":[OSD([sQuery(id+"F6.wireOp",EDGE,"E50.MirrorCS"),sQuery(id+"F6.wireOp",EDGE,"E71.MirrorCS")])]});
            var Q22;
            Q22=makeQuery(id+"F8.opExtrude","SWEPT_EDGE",EDGE,{"disambiguationData":[OSD([sQuery(id+"F6.wireOp",EDGE,"E50.MirrorCS"),sQuery(id+"F6.wireOp",EDGE,"E74.MirrorCS")])]});
            var Q23;
            Q23=makeQuery(id+"F8.opExtrude","SWEPT_EDGE",EDGE,{"disambiguationData":[OSD([sQuery(id+"F6.wireOp",EDGE,"E50.MirrorCS"),sQuery(id+"F6.wireOp",EDGE,"E77.MirrorCS")])]});
            var Q24;
            Q24=makeQuery(id+"F8.opExtrude","SWEPT_EDGE",EDGE,{"disambiguationData":[OSD([sQuery(id+"F6.wireOp",EDGE,"E50.MirrorCS"),sQuery(id+"F6.wireOp",EDGE,"E80.MirrorCS")])]});
            var Q25;
            Q25=makeQuery(id+"F8.opExtrude","SWEPT_EDGE",EDGE,{"disambiguationData":[OSD([sQuery(id+"F6.wireOp",EDGE,"E50.MirrorCS"),sQuery(id+"F6.wireOp",EDGE,"E83.MirrorCS")])]});
            var Q26;
            Q26=makeQuery(id+"F8.opExtrude","SWEPT_EDGE",EDGE,{"disambiguationData":[OSD([sQuery(id+"F6.wireOp",EDGE,"E50.MirrorCS"),sQuery(id+"F6.wireOp",EDGE,"E86.MirrorCS")])]});
            var Q27;
            Q27=makeQuery(id+"F8.opExtrude","SWEPT_EDGE",EDGE,{"disambiguationData":[OSD([sQuery(id+"F6.wireOp",EDGE,"E50.MirrorCS"),sQuery(id+"F6.wireOp",EDGE,"E88.MirrorCS")])]});
            var Q28;
            Q28=makeQuery(id+"F8.opExtrude","SWEPT_EDGE",EDGE,{"disambiguationData":[OSD([sQuery(id+"F6.wireOp",EDGE,"E50.MirrorCS"),sQuery(id+"F6.wireOp",EDGE,"E85.MirrorCS")])]});
            var Q29;
            Q29=makeQuery(id+"F8.opExtrude","SWEPT_EDGE",EDGE,{"disambiguationData":[OSD([sQuery(id+"F6.wireOp",EDGE,"E50.MirrorCS"),sQuery(id+"F6.wireOp",EDGE,"E82.MirrorCS")])]});
            var Q30;
            Q30=makeQuery(id+"F8.opExtrude","SWEPT_EDGE",EDGE,{"disambiguationData":[OSD([sQuery(id+"F6.wireOp",EDGE,"E50.MirrorCS"),sQuery(id+"F6.wireOp",EDGE,"E79.MirrorCS")])]});
            var Q31;
            Q31=makeQuery(id+"F8.opExtrude","SWEPT_EDGE",EDGE,{"disambiguationData":[OSD([sQuery(id+"F6.wireOp",EDGE,"E50.MirrorCS"),sQuery(id+"F6.wireOp",EDGE,"E76.MirrorCS")])]});
            var Q32;
            Q32=makeQuery(id+"F8.opExtrude","SWEPT_EDGE",EDGE,{"disambiguationData":[OSD([sQuery(id+"F6.wireOp",EDGE,"E50.MirrorCS"),sQuery(id+"F6.wireOp",EDGE,"E73.MirrorCS")])]});
            var Q33;
            Q33=makeQuery(id+"F8.opExtrude","SWEPT_EDGE",EDGE,{"disambiguationData":[OSD([sQuery(id+"F6.wireOp",EDGE,"E50.MirrorCS"),sQuery(id+"F6.wireOp",EDGE,"E68.MirrorCS")])]});
            var Q34;
            Q34=makeQuery(id+"F8.opExtrude","SWEPT_EDGE",EDGE,{"disambiguationData":[OSD([sQuery(id+"F6.wireOp",EDGE,"E50.MirrorCS"),sQuery(id+"F6.wireOp",EDGE,"E66.MirrorCS")])]});
            var Q35;
            Q35=makeQuery(id+"F8.opExtrude","SWEPT_EDGE",EDGE,{"disambiguationData":[OSD([sQuery(id+"F6.wireOp",EDGE,"E50.MirrorCS"),sQuery(id+"F6.wireOp",EDGE,"E64.MirrorCS")])]});
            var Q36;
            Q36=makeQuery(id+"F8.opExtrude","SWEPT_EDGE",EDGE,{"disambiguationData":[OSD([sQuery(id+"F6.wireOp",EDGE,"E48"),sQuery(id+"F6.wireOp",EDGE,"E60.1.0.0")])]});
            var Q37;
            Q37=makeQuery(id+"F8.opExtrude","SWEPT_EDGE",EDGE,{"disambiguationData":[OSD([sQuery(id+"F6.wireOp",EDGE,"E48"),sQuery(id+"F6.wireOp",EDGE,"E60.2.0.0")])]});
            var Q38;
            Q38=makeQuery(id+"F8.opExtrude","SWEPT_EDGE",EDGE,{"disambiguationData":[OSD([sQuery(id+"F6.wireOp",EDGE,"E48"),sQuery(id+"F6.wireOp",EDGE,"E60.3.0.0")])]});
            var Q39;
            Q39=makeQuery(id+"F8.opExtrude","SWEPT_EDGE",EDGE,{"disambiguationData":[OSD([sQuery(id+"F6.wireOp",EDGE,"E48"),sQuery(id+"F6.wireOp",EDGE,"E60.4.0.0")])]});
            var Q40;
            Q40=makeQuery(id+"F8.opExtrude","SWEPT_EDGE",EDGE,{"disambiguationData":[OSD([sQuery(id+"F6.wireOp",EDGE,"E48"),sQuery(id+"F6.wireOp",EDGE,"E60.5.0.0")])]});
            var Q41;
            Q41=makeQuery(id+"F8.opExtrude","SWEPT_EDGE",EDGE,{"disambiguationData":[OSD([sQuery(id+"F6.wireOp",EDGE,"E48"),sQuery(id+"F6.wireOp",EDGE,"E60.6.0.0")])]});
            var Q42;
            Q42=makeQuery(id+"F8.opExtrude","SWEPT_EDGE",EDGE,{"disambiguationData":[OSD([sQuery(id+"F6.wireOp",EDGE,"E48"),sQuery(id+"F6.wireOp",EDGE,"E60.7.0.0")])]});
            var Q43;
            Q43=makeQuery(id+"F8.opExtrude","SWEPT_EDGE",EDGE,{"disambiguationData":[OSD([sQuery(id+"F6.wireOp",EDGE,"E48"),sQuery(id+"F6.wireOp",EDGE,"E60.8.0.0")])]});
            fillet(context, id + "F11", {"entities" : qUnion([Q0, Q1, Q2, Q3, Q4, Q5, Q6, Q7, Q8, Q9, Q10, Q11, Q12, Q13, Q14, Q15, Q16, Q17, Q18, Q19, Q20, Q21, Q22, Q23, Q24, Q25, Q26, Q27, Q28, Q29, Q30, Q31, Q32, Q33, Q34, Q35, Q36, Q37, Q38, Q39, Q40, Q41, Q42, Q43]), "radius" : 0.5 * mm, "tangentPropagation" : true, "allowEdgeOverflow" : false});
        }
    });
